# Revit family: Furniture_Tables_Svedholm_Dix-Table
name_source: partatom
category: Furniture
revit_build: Autodesk Revit 2018 (Build: 20190510_1515(x64)
units: mm (PartAtom-declared; Revit-internal decimal feet)

## family parameters
Always vertical = Yes
Cut with Voids When Loaded = No
OmniClass Number = 23.21.23.00
OmniClass Title = Residential Furniture and Equipment
Room Calculation Point = No
Shared = No
Work Plane-Based = Yes

## types (3) — shared parameters
BIMobject category = Tables
Default Elevation = 1219 mm
Description = A side table of wire and glass. Table top of tempered glass with ceramic alternatively marble.
Design country = Sweden
Edition number = 1
IFC Classification = Furniture
Manufacturer = Svedholm
Manufacturer country = Sweden
Manufacturer name = Svedholm
Material main = Glass
Material secondary = Powder coated steel
Model = Dix Table
OmniClass Code = 23-21 23 00
OmniClass Description = Residential Furniture and Equipment
Product Guid = 57d2c32c-0780-4f11-854a-83c862676f14
Product SKU = Dix-table
Product data url = https://bimobject.com
Product family = Dix
Product group = Table
Product name = Dix Table
Product url = https://www.svedholm.se
QR code = https://bimobject.com
Secondary material = Svedholm - Glass - Transparent
UNSPSC Code = 56
URL = https://www.svedholm.se
Uniclass 1.4 Code = L8221
Uniclass 1.4 Description = Tables

## per-type parameters (varying)
| type | Construction 450mm | Marble 900x400mm | Oval 70 x450mm | Round 450mm |
| ART - (203.600.004) Tabletop material - (Marble) | No | Yes | No | No |
| ART - (203.600.001) Tabletop material - (Glass) | Yes | No | No | Yes |
| ART - (203.600.002) Tabletop material - (Glass) | Yes | No | Yes | No |

## geometry (parser evidence)
native form markers: Sweep x6
no freeform markers — native parametric forms only
